# Revit family: Geberit Duofix element for wall-hung WC, 114 cm, with Sigma concealed cistern 8 cm_PRO_219409
name_source: partatom
category: Plumbing Fixtures
revit_build: Autodesk Revit 2018 (Build: 20190510_1515(x64)
units: mm (PartAtom-declared; Revit-internal decimal feet)

## family parameters
Always vertical = Yes
Cut with Voids When Loaded = No
OmniClass Number = 23.45.05.00
OmniClass Title = Sanitary Equipment
Part Type = Normal
Room Calculation Point = Yes
Round Connector Dimension = Use Diameter
Shared = No
Work Plane-Based = No

## types (1)
- 111.698.00.1 Geberit Duofix element for wall-hung WC, 114 cm, with Sigma concealed cistern 8 cm
    ATT_10767 = 0.1 L/s
    CW Connection = Yes
    D = 150 mm
    D1 = 60 mm  [stored 0.19685 ft]
    Description = Geberit Duofix element for wall-hung WC, 114 cm, with Sigma concealed cistern 8 cm
    EAN code basic data = 4025416544319
    Flow pressure = 0.1-10 bar
    Flush volume small, adjustment range = 3-4 l
    Flush volume, factory setting = 4.5 and 3 l
    GEB_connection_diameter1 = 15 mm  [stored 0.0492126 ft]
    GEB_connection_diameter2 = 90 mm  [stored 0.295276 ft]
    GEB_culture = en-AU
    GEB_generic_description = concealed cistern support frame for toilet
    GEB_generic_manufacturer = generic
    GEB_imperial_engineering = No
    GEB_metric_engineering = Yes
    GEB_pimversion = 22.08.08
    GEB_processing_type = T
    GEB_reference = PRO_219409
    GEB_translations = {"ATT_10673":"EAN code basic data","ATT_10773":"Flow pressure","ATT_10811":"Flush volume small, adjustment range","ATT_10832":"Maximum operating temperature, water","ATT_10866":"Flush volume, factory setting"}
    GEB_use_DN = Yes
    H = 1140 mm  [stored 3.74016 ft]
    H1 = 230 mm  [stored 0.754593 ft]
    H2 = 330 mm
    H2_max = 359 mm  [stored 1.17782 ft]
    H2_min = 330 mm
    H3 = 1000 mm  [stored 3.28084 ft]
    HW Connection = No
    IfcDescription = Geberit Duofix element for wall-hung WC, 114 cm, with Sigma concealed cistern 8 cm
    IfcExportAs = IfcSanitaryTerminal
    IfcExportType = CISTERN
    LOD300 = No
    LOD400 = Yes
    Manufacturer = Geberit
    Maximum operating temperature, water = 25 °C
    Model = Sigma 8 cm
    Vent Connection = No
    W = 500 mm  [stored 1.64042 ft]
    Waste Connection = Yes
    Z2_calculated = 226 mm  [stored 0.74147 ft]
    angle_cw = 90.00°
    applicationPurposes = For drywall construction
For installation in part or room-height prewall installations
For installation in room-height installation walls
For wall-hung WCs with connection dimensions for Caroma Cube / Metro / Walvit and Fowler Seido / Lucid
For wall-hung WCs with connection dimensions in accordance with EN 33:2011
For wall-hung WCs with large projection up to 70 cm
For single flush, dual flush or stop-and-go flush
For floor constructions 0–20 cm
    application_range = sanitary systems
    brandName = Geberit
    button_depth = 115 mm  [stored 0.377297 ft]
    characteristics = Range 2016
Self-supporting frame, powder-coated
Frame with ø 9 mm drilling holes for fastening in wood frame construction
Frame suitable for ceramic WC appliances with small contact surface (with pressure-resistant wall covering)
Galvanized feet
Leg supports infinitely variable in height
Non-slip leg supports
Foot plate depth suitable for installation in U-profiles UW 50 and Geberit Duofix system rails
Connection bend can be installed without tools at different depths
Connection bend can be mounted vertically with front flush
Fastening for connection bend, sound-absorbing
Concealed cistern with front actuation
Concealed cistern, fully insulated against condensation
Cistern fulfils standard requirements in accordance with AS 1172.2:2004
Immediate post flush possible with factory setting
Tool-free installation and maintenance work on concealed cistern
Water supply connection on the top left
Water supply connection, dezincification-resistant
Protection cover box for service opening protects against moisture and dirt
Protection box for service opening can be cut to length, suitable for surface-even actuator plates
Equipped with conduit pipe for feed pipe for connection of Geberit AquaClean shower toilets
With fastening option for electrical connection
    cistern_front_offset = 21 mm  [stored 0.0688976 ft]
    cistern_width = 420 mm  [stored 1.37795 ft]
    connection_bend = Yes
    connection_description1 = cold water in
    connection_description2 = sanitary out
    connection_type_c01 = Rp½''
    connection_type_c02 = DN90/ø90 Spigot
    content_date_changed = 2021.12.01
    content_version = GEB MG 1.5
    cw_h = 90 mm  [stored 0.295276 ft]
    cw_orientation = 1
    cw_pos = 200 mm  [stored 0.656168 ft]
    fixed_material = Geberit, Plastic, Opaque white
    fixed_material_01 = Geberit, Steel, Paint Finish, Blue
    fixed_material_02 = Geberit, Laminate, Ivory, Matte
    fixed_material_03 = Geberit, Steel, galvanized
    fixed_material_04 = Geberit, PE-HD, Black
    frame_btm = 1059 mm  [stored 3.47441 ft]
    h1 = 504 mm  [stored 1.65354 ft]
    key 1000 = 111.698.00.1
    name = Geberit Duofix element for wall-hung WC, 114 cm, with Sigma concealed cistern 8 cm
    outlet_flow = 0.0 L/s
    productBrand = Duofix
    rod_width_180 = 180 mm  [stored 0.590551 ft]
    rod_width_280 = 280 mm  [stored 0.918635 ft]
    sanitary socket = No
    scopeOfDelivery = Water supply connection Rp 1/2" - R 1/2", compatible with MF, with integrated angle stop valve and hand wheel
Protection box for service opening
Connection set for WC, ø 90 mm
Connection bend 90° made of PE-HD, ø 90 mm
Sleeve made of EPDM, ø 90 / 110 mm
Pipe bracket support
2 protection plugs
2 threaded rods M12
Fastening material
    supply_connection_warning = Reducer connected to element not required and should not be accounted for in a BOM
    type = Sigma 8 cm
    wt_h = 43 mm  [stored 0.141076 ft]

note: [stored X ft] marks values corroborated as IEEE doubles in the binary element streams (Revit-internal decimal feet)

## geometry (parser evidence)
native form markers: Blend x6, Sweep x5
no freeform markers — native parametric forms only
